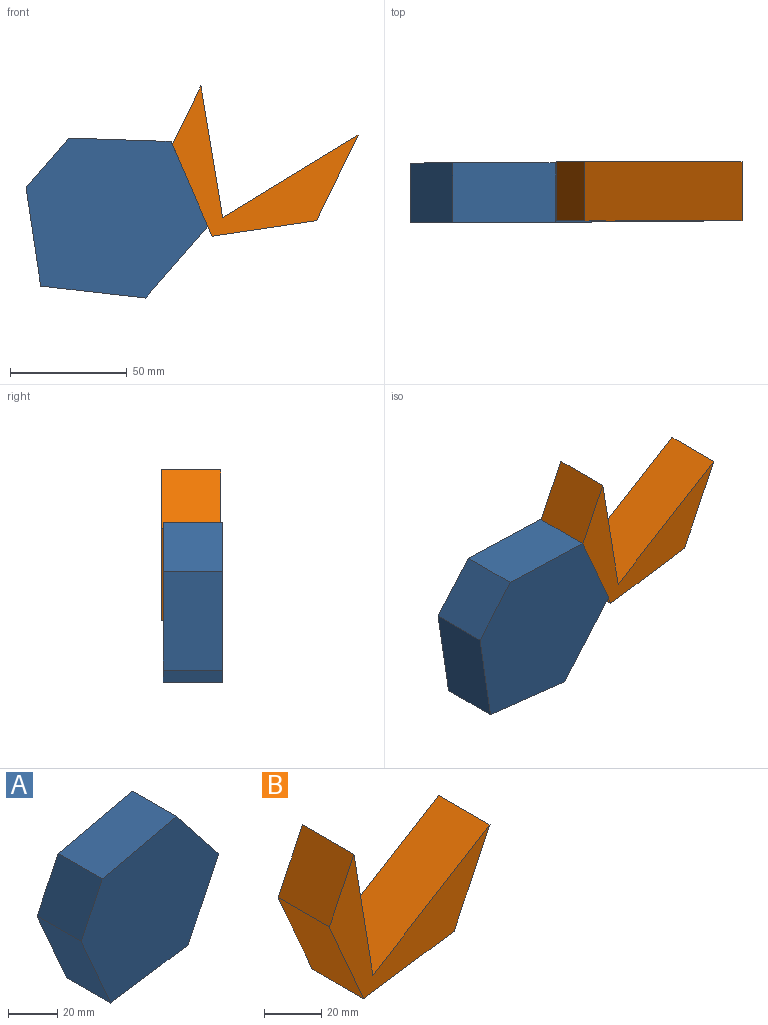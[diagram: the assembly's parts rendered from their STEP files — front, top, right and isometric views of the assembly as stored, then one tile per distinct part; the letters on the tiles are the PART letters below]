
ASSEMBLY  parts=2 mates=1
PART A: 8 faces, bbox 79.5x25.4x74.3 mm
  f0: plane 25.4x25.16mm, normal (-0.9,0,0.44), area 710.3mm2, adj f1,f5,f6,f7
  f1: plane 39.22x25.4mm, normal (-0.92,0,-0.4), area 1085.8mm2, adj f0,f2,f6,f7
  f2: plane 44.77x25.4mm, normal (0.15,0,-0.99), area 1149.6mm2, adj f1,f3,f6,f7
  f3: plane 36.63x25.4mm, normal (0.9,0,-0.44), area 1033.9mm2, adj f2,f4,f6,f7
  f4: plane 30.99x25.4mm, normal (0.78,0,0.62), area 1004.7mm2, adj f3,f5,f6,f7
  f5: plane 42.75x25.4mm, normal (-0.23,0,0.97), area 1114.6mm2, adj f0,f4,f6,f7
  f6: plane 79.54x74.27mm, normal (0,-1,0), area 4114.8mm2, adj f0,f1,f2,f3,f4,f5
  f7: plane 79.54x74.27mm, normal (0,1,0), area 4114.8mm2, adj f0,f1,f2,f3,f4,f5
PART B: 8 faces, bbox 79.5x25.4x64.4 mm
  f0: plane 25.4x25.16mm, normal (-0.9,0,0.44), area 710.3mm2, adj f1,f5,f6,f7
  f1: plane 39.22x25.4mm, normal (-0.92,0,-0.4), area 1085.8mm2, adj f0,f2,f6,f7
  f2: plane 44.77x25.4mm, normal (0.15,0,-0.99), area 1149.6mm2, adj f1,f3,f6,f7
  f3: plane 36.63x25.4mm, normal (0.9,0,-0.44), area 1033.9mm2, adj f2,f4,f6,f7
  f4: plane 58x35.38mm, normal (-0.52,0,0.85), area 1725.7mm2, adj f3,f5,f6,f7
  f5: plane 56.47x25.4mm, normal (0.99,0,0.16), area 1453.8mm2, adj f0,f4,f6,f7
  f6: plane 79.54x64.37mm, normal (0,-1,0), area 1527.9mm2, adj f0,f1,f2,f3,f4,f5
  f7: plane 79.54x64.37mm, normal (0,1,0), area 1527.9mm2, adj f0,f1,f2,f3,f4,f5
PLACE A rot(axis=(0,1,0),15deg) t=(-44.97,-3.28,1.3)mm
PLACE B t=(23.24,-2.7,30.05)mm
MATE planar A.f4 <-> B.f1  axis (0.92,0,0.4) through (-11.93,-15.98,28.9)mm
